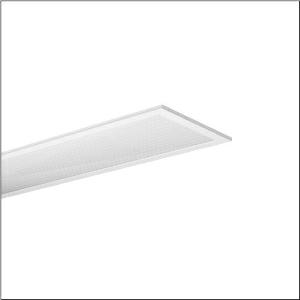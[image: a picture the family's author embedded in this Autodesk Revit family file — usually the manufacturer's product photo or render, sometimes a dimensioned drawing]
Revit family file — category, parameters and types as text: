
# Revit family: apollon_r__21_linear_51mq17wd2312_219c
name_source: partatom
category: Lighting Fixtures
units: mm (PartAtom-declared; Revit-internal decimal feet)

## family parameters
Cut with Voids When Loaded = No
Host = Face
Light Source = No
Part Type = Normal
Room Calculation Point = No
Round Connector Dimension = Use Diameter
Shared = No

## types (1)
- Apollon® 21 linear (1 x LED, 6900 lm, 60 W, 3000K)
    Apparent Load = 60 VA
    CIE Flux Codes = 61 87 97 100 100
    Color Rendering = 80
    Color Temperature = 3000K
    Default Elevation = 1800 mm
    Description = Apollon® 21 linear, office luminaire, primary optical cover: micro prismatic cover, CAT 2 (L<= 3000cd/m²), light emission: direct distribution, primary light characteristic: symmetric, installation type: lay-in mounting, LED, rated luminous flux: 6.900lm, luminous efficacy: 115lm/W, light colour: 830, colour temperature: 3000K, with terminal, 5-pole, mains connection: 220..240V, AC, 50/60Hz, rated input power: 60W, housing, of aluminium, coated, pure white, length: 1.545mm, width: 307mm, height: 39mm, housing upper side, of sheet steel, galvanised, protection rating (complete): IP20, protection rating (lamp compartment, on room side): IP50, insulation class (complete): insulation class II (safety insulation), certification: CE, ENEC, packaging unit: 1 piece
    Height = 0 mm  [stored 0 ft]
    Lamp = 1 x LED
    Lamp Light Flux = 6900 lm
    Lamp Power = 60 W
    Lamp count = 1
    Length = 1545 mm
    Luminous efficacy = 115 lm/W
    Manufacturer = Siteco
    ModVariant = No
    Model = 51MQ17WD2312
    Mounting Place = Ceiling
    Mounting Type = Recessed
    Number of Poles = 1
    OnlyDefault = Yes
    Power Factor = 1
    Product Name = Apollon® 21 linear
    Product group = office luminaire | ceiling recessed
    ProductGroupID = 401
    Protection Class = Protection class II
    Protection Degree = IP 20
    RLX_Detail_Level = 1
    RLX_Emergency_Light_Flux = 0 lm
    RLX_Emergency_Type = 0
    RLX_Emergency_Type_DB = No
    RlxData = <blob elided: 17205 chars, md5=5828c64b>
    Socket = socket
    Standby Power = 0 W
    System Light Flux = 6900 lm
    System Power = 60 W
    Type Comments = Product without accessories
    Type Image = l_1291045.jpg
    URL = http://relux.com
    VarID = ---
    Voltage = 0 V
    Weight = 0.00 kg
    Width = 307 mm

note: [stored X ft] marks values corroborated as IEEE doubles in the binary element streams (Revit-internal decimal feet)

## geometry (parser evidence)
native form markers: Blend x4, Sweep x9
no freeform markers — native parametric forms only
